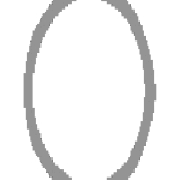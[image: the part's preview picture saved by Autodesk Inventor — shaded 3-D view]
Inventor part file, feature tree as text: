
AUTODESK INVENTOR PART (.ipt)
format: ipt  version: 2021 (Build 250183000, 183)  size: 113,152 bytes
history: native  units: in
note: dims shown in document units (in); Inventor stores cm internally (conversion verified against a paired STEP export)
features: other x4, sketch x3, plane x1
ambient origin geometry x8: Origin, YZ Plane, XZ Plane, XY Plane, X Axis, Y Axis, Z Axis, Center Point
bodies: Solid1 (feature_tree), Body (feature_tree)
feature tree (8):
  other  "Driven Length"
  other  "Frame Generator"
  other  "Start Plane"
  other  "End Plane"
  sketch  "Sketch"  dims[d2=16.0in d4=-0.0in d5=16.0in d6=0.12in d7=0.0in d8=90.0deg d9=16.0in]
  sketch  "Sketch2"  dims[d0=1.0in]
  plane  "Work Plane3"
  sketch  "Sketch3"  dims[d1=0.065in]
